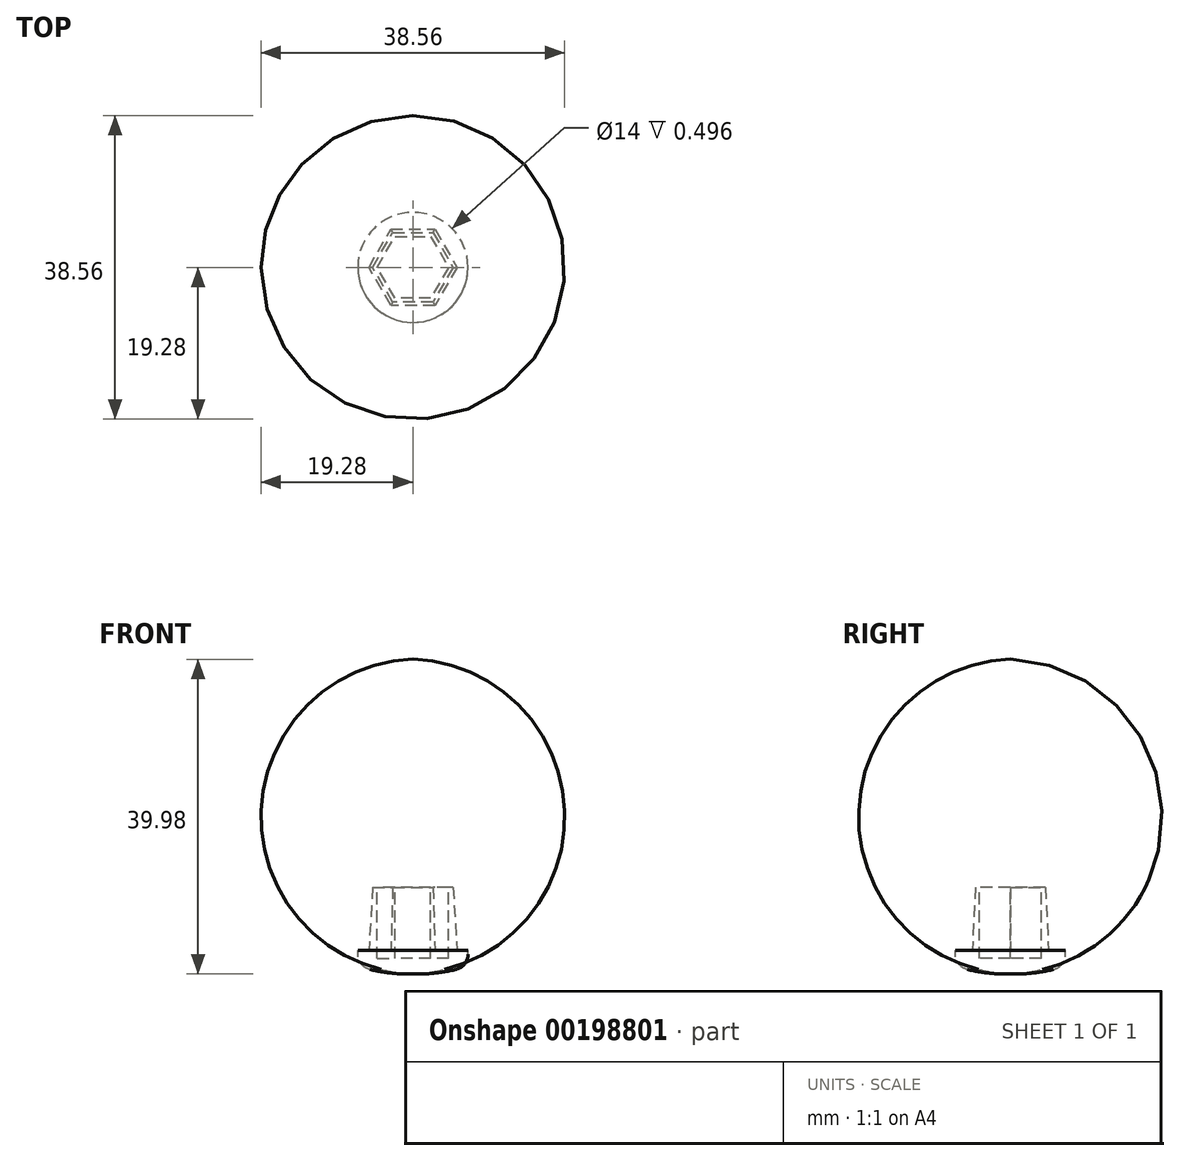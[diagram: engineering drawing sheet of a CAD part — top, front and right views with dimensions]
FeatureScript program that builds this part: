
annotation { "Feature Type Name" : "Feature", "Feature Type Description" : "" }
export const myFeature = defineFeature(function(context is Context, id is Id, definition is map)
    precondition{}
    {
        {
            var Q0;
            Q0=qCreatedBy(makeId("Front.planeOp"),FACE);
            var sketch = newSketch(context, id + "F0", { "sketchPlane" : qUnion([Q0])});
            skLineSegment(sketch, "E0", {"start": v(0, 0) * mm, "end": v(-7, 0) * mm});
            skLineSegment(sketch, "E1", {"start": v(0, 0) * mm, "end": v(0, -3) * mm});
            skLineSegment(sketch, "E2", {"start": v(-7, 0) * mm, "end": v(-7, -2) * mm});
            skArc(sketch, "E3", {"start": v(-7, -2) * mm, "mid": v(-3.54, -2.81) * mm, "end": v(0, -3) * mm});
            skPoint(sketch, "E4.orphan", {"position": v(5.57, -2) * mm});
            skSolve(sketch);
        }
        {
            var Q0;
            Q0 = qSketchRegion(id + "F0", true);
            var Q1;
            Q1=sQuery(id+"F0.wireOp",EDGE,"E1");
            revolve(context, id + "F1", {"entities" : qUnion([Q0]), "axis" : qUnion([Q1]), "revolveType" : RevolveType.FULL});
        }
        {
            var Q0;
            Q0=makeQuery(id+"F1.opRevolve","SWEPT_FACE",FACE,{"disambiguationData":[OSD([sQuery(id+"F0.wireOp",EDGE,"E0")])]});
            var sketch = newSketch(context, id + "F2", { "sketchPlane" : qUnion([Q0])});
            skCircle(sketch, "E5.cCircle", {"center": v(0, 0) * mm, "radius": 4.85 * mm, "construction": true});
            skLineSegment(sketch, "E5.0", {"start": v(5.6, 0) * mm, "end": v(2.8, -4.85) * mm});
            skLineSegment(sketch, "E5.1", {"start": v(2.8, -4.85) * mm, "end": v(-2.8, -4.85) * mm});
            skLineSegment(sketch, "E5.2", {"start": v(-2.8, -4.85) * mm, "end": v(-5.6, 0) * mm});
            skLineSegment(sketch, "E5.3", {"start": v(-5.6, 0) * mm, "end": v(-2.8, 4.85) * mm});
            skLineSegment(sketch, "E5.4", {"start": v(-2.8, 4.85) * mm, "end": v(2.8, 4.85) * mm});
            skLineSegment(sketch, "E5.5", {"start": v(2.8, 4.85) * mm, "end": v(5.6, 0) * mm});
            skPoint(sketch, "E5.0.midPoint", {"position": v(4.2, -2.42) * mm});
            skSolve(sketch);
        }
        {
            var Q0;
            Q0 = qSketchRegion(id + "F2", true);
            extrude(context, id + "F3", {"entities" : qUnion([Q0]), "operationType" : NewBodyOperationType.ADD, "depth" : 8 * mm, "hasDraft" : true, "draftAngle" : 3 * degree, "draftPullDirection" : true});
        }
        {
            var Q0;
            Q0=makeQuery(id+"F1.opRevolve","SWEPT_EDGE",EDGE,{"disambiguationData":[OSD([sQuery(id+"F0.wireOp",EDGE,"E2"),sQuery(id+"F0.wireOp",EDGE,"E3")])]});
            fillet(context, id + "F4", {"entities" : qUnion([Q0]), "radius" : 2 * mm, "tangentPropagation" : true, "allowEdgeOverflow" : false});
        }
        {
            var Q0;
            Q0=makeQuery(id+"F3.opExtrude","CAP_FACE",FACE,{"disambiguationData":[OSD([sQuery(id+"F2.wireOp",EDGE,"E5.0"),sQuery(id+"F2.wireOp",EDGE,"E5.1"),sQuery(id+"F2.wireOp",EDGE,"E5.2"),sQuery(id+"F2.wireOp",EDGE,"E5.3"),sQuery(id+"F2.wireOp",EDGE,"E5.4"),sQuery(id+"F2.wireOp",EDGE,"E5.5")])],"isStart":false});
            var sketch = newSketch(context, id + "F5", { "sketchPlane" : qUnion([Q0])});
            skCircle(sketch, "E6.cCircle", {"center": v(0, 0) * mm, "radius": 3.93 * mm, "construction": true});
            skLineSegment(sketch, "E6.0", {"start": v(2.27, -3.93) * mm, "end": v(-2.27, -3.93) * mm});
            skLineSegment(sketch, "E6.1", {"start": v(-2.27, -3.93) * mm, "end": v(-4.54, 0) * mm});
            skLineSegment(sketch, "E6.2", {"start": v(-4.54, 0) * mm, "end": v(-2.27, 3.93) * mm});
            skLineSegment(sketch, "E6.3", {"start": v(-2.27, 3.93) * mm, "end": v(2.27, 3.93) * mm});
            skLineSegment(sketch, "E6.4", {"start": v(2.27, 3.93) * mm, "end": v(4.54, 0) * mm});
            skLineSegment(sketch, "E6.5", {"start": v(4.54, 0) * mm, "end": v(2.27, -3.93) * mm});
            skPoint(sketch, "E6.0.midPoint", {"position": v(0, -3.93) * mm});
            skSolve(sketch);
        }
        {
            var Q0;
            Q0 = qSketchRegion(id + "F5", true);
            extrude(context, id + "F6", {"entities" : qUnion([Q0]), "operationType" : NewBodyOperationType.REMOVE, "oppositeDirection" : true, "depth" : 9.06 * mm});
        }
    });
